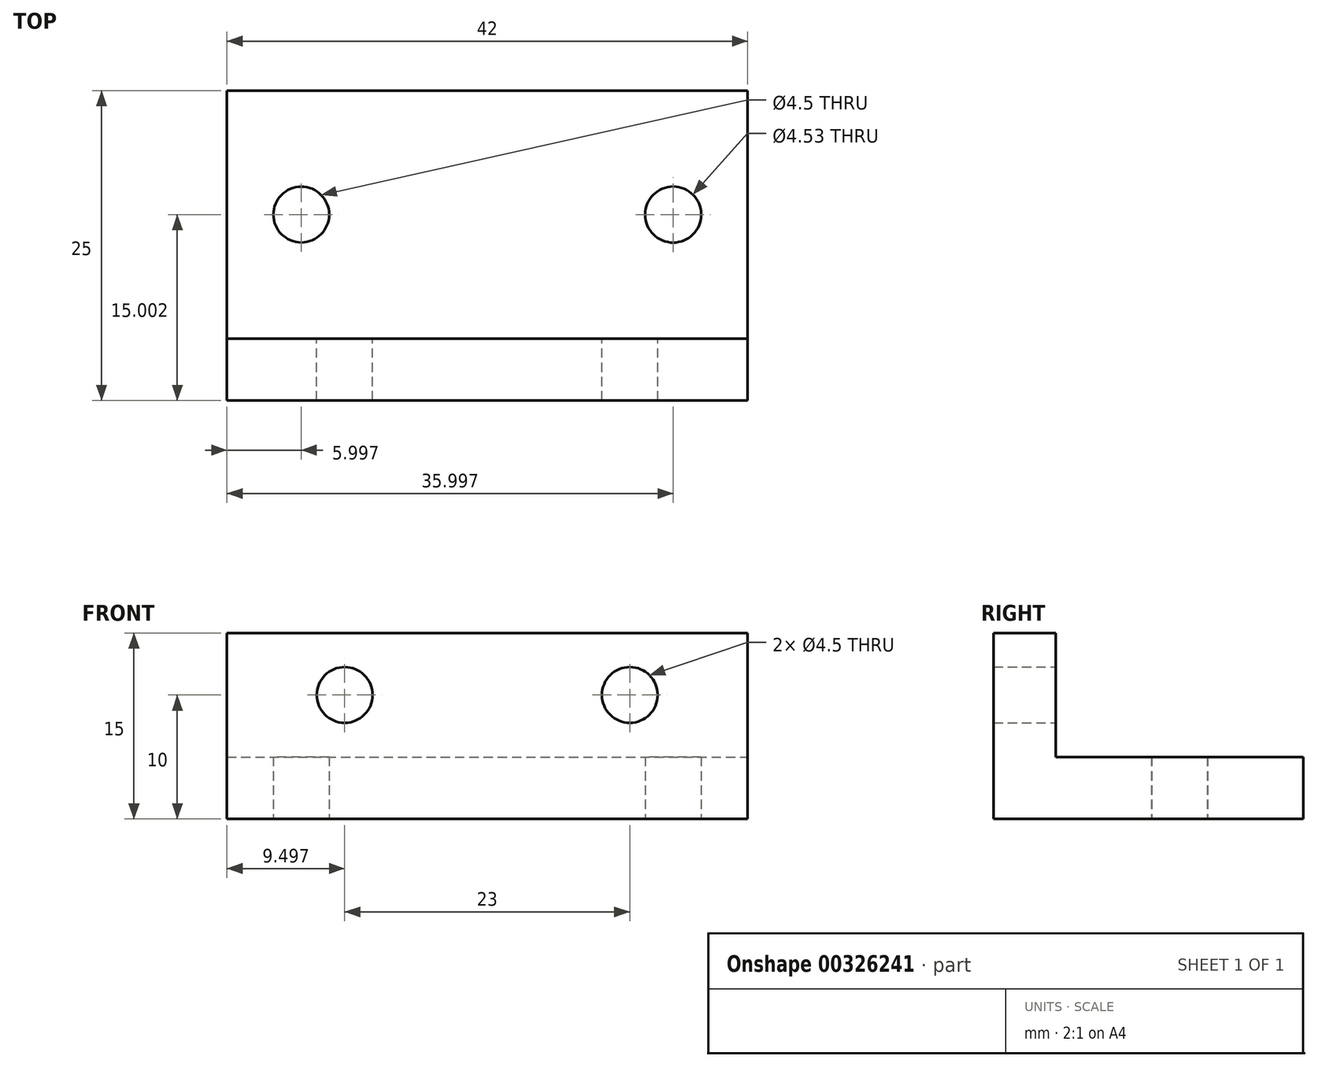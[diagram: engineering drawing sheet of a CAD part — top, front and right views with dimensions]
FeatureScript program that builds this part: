
annotation { "Feature Type Name" : "Feature", "Feature Type Description" : "" }
export const myFeature = defineFeature(function(context is Context, id is Id, definition is map)
    precondition{}
    {
        {
            var Q0;
            Q0=qCreatedBy(makeId("Top.planeOp"),FACE);
            var sketch = newSketch(context, id + "F0", { "sketchPlane" : qUnion([Q0])});
            skLineSegment(sketch, "E0.bottom", {"start": v(-19.36, 10.26) * mm, "end": v(22.64, 10.26) * mm});
            skLineSegment(sketch, "E0.top", {"start": v(-19.36, -14.74) * mm, "end": v(22.64, -14.74) * mm});
            skLineSegment(sketch, "E0.left", {"start": v(-19.36, 10.26) * mm, "end": v(-19.36, -14.74) * mm});
            skLineSegment(sketch, "E0.right", {"start": v(22.64, 10.26) * mm, "end": v(22.64, -14.74) * mm});
            skLineSegment(sketch, "E1", {"start": v(-19.36, -9.74) * mm, "end": v(22.64, -9.74) * mm});
            skCircle(sketch, "E2", {"center": v(-13.36, 0.26) * mm, "radius": 2.25 * mm});
            skCircle(sketch, "E3", {"center": v(16.64, 0.26) * mm, "radius": 2.26 * mm});
            skSolve(sketch);
        }
        {
            var Q0;
            Q0=qSketchRegion(id+"F0",true);
            extrude(context, id + "F1", {"entities" : qUnion([Q0]), "depth" : 5 * mm});
        }
        {
            var Q0;
            {var subQ0=sQuery(id+"F0.wireOp",EDGE,"E0.top");Q0=makeQuery(id+"F0.imprint","IMPRINT",FACE,{"disambiguationData":[TD([[makeQuery(id+"F0.imprint","IMPRINT",EDGE,{"derivedFrom":subQ0}),1.0]])]});}
            extrude(context, id + "F2", {"entities" : qUnion([Q0]), "operationType" : NewBodyOperationType.ADD, "depth" : 15 * mm});
        }
        {
            var Q0;
            Q0=makeQuery(id+"F2.opExtrude","SWEPT_FACE",FACE,{"disambiguationData":[OSD([sQuery(id+"F0.wireOp",EDGE,"E1")])]});
            var sketch = newSketch(context, id + "F3", { "sketchPlane" : qUnion([Q0])});
            skCircle(sketch, "E4", {"center": v(-13.14, 10) * mm, "radius": 2.25 * mm});
            skPoint(sketch, "E4.centerSnap0", {"position": v(-22.64, 10) * mm});
            skCircle(sketch, "E5", {"center": v(9.86, 10) * mm, "radius": 2.25 * mm});
            skSolve(sketch);
        }
        {
            var Q0;
            Q0=qSketchRegion(id+"F3",true);
            extrude(context, id + "F4", {"entities" : qUnion([Q0]), "operationType" : NewBodyOperationType.REMOVE, "oppositeDirection" : true, "depth" : 10 * mm});
        }
    });
